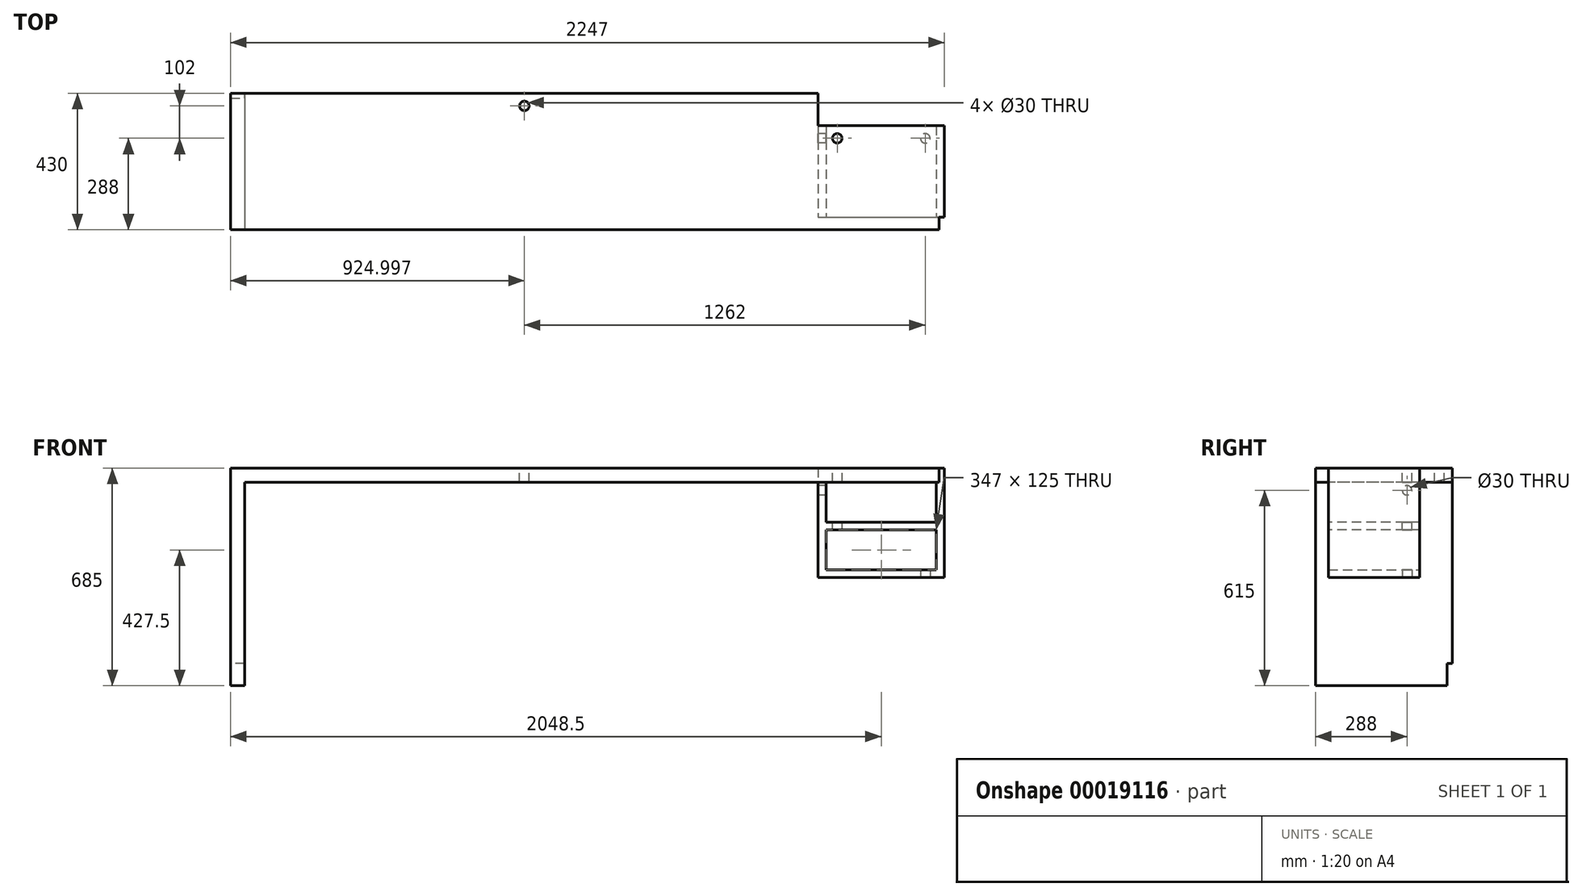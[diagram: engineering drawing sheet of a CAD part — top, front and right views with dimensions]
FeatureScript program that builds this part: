
annotation { "Feature Type Name" : "Feature", "Feature Type Description" : "" }
export const myFeature = defineFeature(function(context is Context, id is Id, definition is map)
    precondition{}
    {
        {
            var Q0;
            Q0=qCreatedBy(makeId("Top.planeOp"),FACE);
            var sketch = newSketch(context, id + "F0", { "sketchPlane" : qUnion([Q0])});
            skLineSegment(sketch, "E0.bottom", {"start": v(-253.01, 247.5) * mm, "end": v(1596.99, 247.5) * mm});
            skLineSegment(sketch, "E0.left", {"start": v(-253.01, 247.5) * mm, "end": v(-253.01, -182.5) * mm});
            skLineSegment(sketch, "E1", {"start": v(-253.01, -182.5) * mm, "end": v(1993.99, -182.5) * mm, "construction": true});
            skLineSegment(sketch, "E2", {"start": v(1596.99, 247.5) * mm, "end": v(1596.99, 145.5) * mm});
            skLineSegment(sketch, "E3", {"start": v(1596.99, 145.5) * mm, "end": v(1993.99, 145.5) * mm});
            skLineSegment(sketch, "E4", {"start": v(1993.99, -182.5) * mm, "end": v(1993.99, 145.5) * mm, "construction": true});
            skLineSegment(sketch, "E5", {"start": v(1993.99, -142.5) * mm, "end": v(1977.99, -142.5) * mm});
            skLineSegment(sketch, "E6", {"start": v(1977.99, -142.5) * mm, "end": v(1977.99, -182.5) * mm});
            skLineSegment(sketch, "E7", {"start": v(1993.99, 145.5) * mm, "end": v(1993.99, -142.5) * mm});
            skLineSegment(sketch, "E8", {"start": v(-253.01, -182.5) * mm, "end": v(1977.99, -182.5) * mm});
            skSolve(sketch);
        }
        {
            var Q0;
            Q0 = qSketchRegion(id + "F0", true);
            extrude(context, id + "F1", {"entities" : qUnion([Q0]), "depth" : 45 * mm});
        }
        {
            var Q0;
            Q0=makeQuery(id+"F1.opExtrude","CAP_FACE",FACE,{"disambiguationData":[OSD([sQuery(id+"F0.wireOp",EDGE,"E0.bottom"),sQuery(id+"F0.wireOp",EDGE,"E0.left"),sQuery(id+"F0.wireOp",EDGE,"E1"),sQuery(id+"F0.wireOp",EDGE,"E2"),sQuery(id+"F0.wireOp",EDGE,"E3"),sQuery(id+"F0.wireOp",EDGE,"E4")])],"isStart":true});
            var sketch = newSketch(context, id + "F2", { "sketchPlane" : qUnion([Q0])});
            skLineSegment(sketch, "E9.bottom", {"start": v(-253.01, -247.5) * mm, "end": v(-208.01, -247.5) * mm});
            skLineSegment(sketch, "E9.top", {"start": v(-253.01, 182.5) * mm, "end": v(-208.01, 182.5) * mm});
            skLineSegment(sketch, "E9.left", {"start": v(-253.01, -247.5) * mm, "end": v(-253.01, 182.5) * mm});
            skLineSegment(sketch, "E9.right", {"start": v(-208.01, -247.5) * mm, "end": v(-208.01, 182.5) * mm});
            skSolve(sketch);
        }
        {
            var Q0;
            Q0 = qSketchRegion(id + "F2", true);
            extrude(context, id + "F3", {"entities" : qUnion([Q0]), "operationType" : NewBodyOperationType.ADD, "depth" : 640 * mm});
        }
        {
            var Q0;
            Q0=makeQuery(id+"F3.boolean.opBoolean","MERGE",FACE,{"derivedFrom":[makeQuery(id+"F1.opExtrude","SWEPT_FACE",FACE,{"disambiguationData":[OSD([sQuery(id+"F0.wireOp",EDGE,"E0.bottom")])]}),makeQuery(id+"F3.opExtrude","SWEPT_FACE",FACE,{"disambiguationData":[OSD([sQuery(id+"F2.wireOp",EDGE,"1aea196a-26a9-4693-80b4-0dba0a0e35e5.top")])]})]});
            var sketch = newSketch(context, id + "F4", { "sketchPlane" : qUnion([Q0])});
            skLineSegment(sketch, "E10.bottom", {"start": v(208.01, -640) * mm, "end": v(253.01, -640) * mm});
            skLineSegment(sketch, "E10.top", {"start": v(208.01, -570) * mm, "end": v(253.01, -570) * mm});
            skLineSegment(sketch, "E10.left", {"start": v(208.01, -640) * mm, "end": v(208.01, -570) * mm});
            skLineSegment(sketch, "E10.right", {"start": v(253.01, -640) * mm, "end": v(253.01, -570) * mm});
            skSolve(sketch);
        }
        {
            var Q0;
            Q0 = qSketchRegion(id + "F4", true);
            extrude(context, id + "F5", {"entities" : qUnion([Q0]), "operationType" : NewBodyOperationType.REMOVE, "oppositeDirection" : true, "depth" : 16 * mm});
        }
        {
            var Q0;
            Q0=makeQuery(id+"F1.opExtrude","CAP_FACE",FACE,{"disambiguationData":[OSD([sQuery(id+"F0.wireOp",EDGE,"E0.bottom"),sQuery(id+"F0.wireOp",EDGE,"E0.left"),sQuery(id+"F0.wireOp",EDGE,"E1"),sQuery(id+"F0.wireOp",EDGE,"E2"),sQuery(id+"F0.wireOp",EDGE,"E3"),sQuery(id+"F0.wireOp",EDGE,"E4")])],"isStart":true});
            var sketch = newSketch(context, id + "F6", { "sketchPlane" : qUnion([Q0])});
            skLineSegment(sketch, "E11.bottom", {"start": v(1993.99, 142.5) * mm, "end": v(1968.99, 142.5) * mm});
            skLineSegment(sketch, "E11.top", {"start": v(1993.99, -145.5) * mm, "end": v(1968.99, -145.5) * mm});
            skLineSegment(sketch, "E11.left", {"start": v(1993.99, 142.5) * mm, "end": v(1993.99, -145.5) * mm});
            skLineSegment(sketch, "E11.right", {"start": v(1968.99, 142.5) * mm, "end": v(1968.99, -145.5) * mm});
            skLineSegment(sketch, "E12.bottom", {"start": v(1596.99, -145.5) * mm, "end": v(1621.99, -145.5) * mm});
            skLineSegment(sketch, "E12.top", {"start": v(1596.99, 142.5) * mm, "end": v(1621.99, 142.5) * mm});
            skLineSegment(sketch, "E12.left", {"start": v(1596.99, -145.5) * mm, "end": v(1596.99, 142.5) * mm});
            skLineSegment(sketch, "E12.right", {"start": v(1621.99, -145.5) * mm, "end": v(1621.99, 142.5) * mm});
            skSolve(sketch);
        }
        {
            var Q0;
            Q0 = qSketchRegion(id + "F6", true);
            extrude(context, id + "F7", {"entities" : qUnion([Q0]), "operationType" : NewBodyOperationType.ADD, "depth" : 275 * mm});
        }
        {
            var Q0;
            Q0=makeQuery(id+"F7.opExtrude","CAP_FACE",FACE,{"disambiguationData":[OSD([sQuery(id+"F6.wireOp",EDGE,"E12.bottom"),sQuery(id+"F6.wireOp",EDGE,"E12.top"),sQuery(id+"F6.wireOp",EDGE,"E12.left"),sQuery(id+"F6.wireOp",EDGE,"E12.right")])],"isStart":false});
            var sketch = newSketch(context, id + "F8", { "sketchPlane" : qUnion([Q0])});
            skLineSegment(sketch, "E13.bottom", {"start": v(1596.99, 142.5) * mm, "end": v(1993.99, 142.5) * mm});
            skLineSegment(sketch, "E13.top", {"start": v(1596.99, -145.5) * mm, "end": v(1993.99, -145.5) * mm});
            skLineSegment(sketch, "E13.left", {"start": v(1596.99, 142.5) * mm, "end": v(1596.99, -145.5) * mm});
            skLineSegment(sketch, "E13.right", {"start": v(1993.99, 142.5) * mm, "end": v(1993.99, -145.5) * mm});
            skSolve(sketch);
        }
        {
            var Q0;
            Q0 = qSketchRegion(id + "F8", true);
            extrude(context, id + "F9", {"entities" : qUnion([Q0]), "operationType" : NewBodyOperationType.ADD, "depth" : 25 * mm});
        }
        {
            var Q0;
            Q0=makeQuery(id+"F9.boolean.opBoolean","MERGE",FACE,{"derivedFrom":[makeQuery(id+"F7.boolean.opBoolean","MERGE",FACE,{"derivedFrom":[makeQuery(id+"F3.boolean.opBoolean","MERGE",FACE,{"derivedFrom":[makeQuery(id+"F1.opExtrude","SWEPT_FACE",FACE,{"disambiguationData":[OSD([sQuery(id+"F0.wireOp",EDGE,"E1")])]}),makeQuery(id+"F3.opExtrude","SWEPT_FACE",FACE,{"disambiguationData":[OSD([sQuery(id+"F2.wireOp",EDGE,"1aea196a-26a9-4693-80b4-0dba0a0e35e5.bottom")])]})]}),makeQuery(id+"F7.opExtrude","SWEPT_FACE",FACE,{"disambiguationData":[OSD([sQuery(id+"F6.wireOp",EDGE,"E11.bottom")])]}),makeQuery(id+"F7.opExtrude","SWEPT_FACE",FACE,{"disambiguationData":[OSD([sQuery(id+"F6.wireOp",EDGE,"E12.top")])]})]}),makeQuery(id+"F9.opExtrude","SWEPT_FACE",FACE,{"disambiguationData":[OSD([sQuery(id+"F8.wireOp",EDGE,"E13.bottom")])]})]});
            var sketch = newSketch(context, id + "F10", { "sketchPlane" : qUnion([Q0])});
            skLineSegment(sketch, "E14.bottom", {"start": v(1621.99, -125) * mm, "end": v(1968.99, -125) * mm});
            skLineSegment(sketch, "E14.top", {"start": v(1621.99, -150) * mm, "end": v(1968.99, -150) * mm});
            skLineSegment(sketch, "E14.left", {"start": v(1621.99, -125) * mm, "end": v(1621.99, -150) * mm});
            skLineSegment(sketch, "E14.right", {"start": v(1968.99, -125) * mm, "end": v(1968.99, -150) * mm});
            skSolve(sketch);
        }
        {
            var Q0;
            Q0 = qSketchRegion(id + "F10", true);
            extrude(context, id + "F11", {"entities" : qUnion([Q0]), "operationType" : NewBodyOperationType.ADD, "oppositeDirection" : true, "depth" : 288 * mm});
        }
        {
            var Q0;
            Q0=makeQuery(id+"F9.opExtrude","CAP_FACE",FACE,{"disambiguationData":[OSD([sQuery(id+"F8.wireOp",EDGE,"E13.bottom"),sQuery(id+"F8.wireOp",EDGE,"E13.top"),sQuery(id+"F8.wireOp",EDGE,"E13.left"),sQuery(id+"F8.wireOp",EDGE,"E13.right")])],"isStart":false});
            var sketch = newSketch(context, id + "F12", { "sketchPlane" : qUnion([Q0])});
            skLineSegment(sketch, "E15", {"start": v(1933.99, 142.5) * mm, "end": v(1933.99, -145.5) * mm, "construction": true});
            skCircle(sketch, "E16", {"center": v(1933.99, -105.5) * mm, "radius": 15 * mm});
            skSolve(sketch);
        }
        {
            var Q0;
            Q0 = qSketchRegion(id + "F12", true);
            extrude(context, id + "F13", {"entities" : qUnion([Q0]), "operationType" : NewBodyOperationType.REMOVE, "endBound" : BoundingType.UP_TO_NEXT, "oppositeDirection" : true, "depth" : 25 * mm});
        }
        {
            var Q0;
            Q0=makeQuery(id+"F1.opExtrude","CAP_FACE",FACE,{"disambiguationData":[OSD([sQuery(id+"F0.wireOp",EDGE,"E0.bottom"),sQuery(id+"F0.wireOp",EDGE,"E0.left"),sQuery(id+"F0.wireOp",EDGE,"E1"),sQuery(id+"F0.wireOp",EDGE,"E2"),sQuery(id+"F0.wireOp",EDGE,"E3"),sQuery(id+"F0.wireOp",EDGE,"E4")])],"isStart":false});
            var sketch = newSketch(context, id + "F14", { "sketchPlane" : qUnion([Q0])});
            skLineSegment(sketch, "E17", {"start": v(671.99, 247.5) * mm, "end": v(671.99, -182.5) * mm, "construction": true});
            skCircle(sketch, "E18", {"center": v(671.99, 207.5) * mm, "radius": 15 * mm});
            skLineSegment(sketch, "E19", {"start": v(1656.99, 145.5) * mm, "end": v(1656.99, -182.5) * mm, "construction": true});
            skCircle(sketch, "E20", {"center": v(1656.99, 105.5) * mm, "radius": 15 * mm});
            skSolve(sketch);
        }
        {
            var Q0;
            Q0 = qSketchRegion(id + "F14", true);
            extrude(context, id + "F15", {"entities" : qUnion([Q0]), "operationType" : NewBodyOperationType.REMOVE, "oppositeDirection" : true, "depth" : 253.52 * mm});
        }
        {
            var Q0;
            Q0=makeQuery(id+"F9.boolean.opBoolean","MERGE",FACE,{"derivedFrom":[makeQuery(id+"F7.opExtrude","SWEPT_FACE",FACE,{"disambiguationData":[OSD([sQuery(id+"F6.wireOp",EDGE,"E12.left")])]}),makeQuery(id+"F9.opExtrude","SWEPT_FACE",FACE,{"disambiguationData":[OSD([sQuery(id+"F8.wireOp",EDGE,"E13.left")])]})]});
            var sketch = newSketch(context, id + "F16", { "sketchPlane" : qUnion([Q0])});
            skLineSegment(sketch, "E21", {"start": v(-145.5, -25) * mm, "end": v(142.5, -25) * mm, "construction": true});
            skCircle(sketch, "E22", {"center": v(-105.5, -25) * mm, "radius": 15 * mm});
            skSolve(sketch);
        }
        {
            var Q0;
            Q0 = qSketchRegion(id + "F16", true);
            extrude(context, id + "F17", {"entities" : qUnion([Q0]), "operationType" : NewBodyOperationType.REMOVE, "endBound" : BoundingType.UP_TO_NEXT, "oppositeDirection" : true, "depth" : 25 * mm});
        }
    });
